# Revit family: Plate_System_Water_Coolers-Zurn-Industries_Z1217
name_source: partatom
category: Plumbing Fixtures
units: mm (PartAtom-declared; Revit-internal decimal feet)

## family parameters
Cut with Voids When Loaded = No
Host = Face
Maintain Annotation Orientation = No
OmniClass Number = 23.45.55.11
OmniClass Title = Sanitary Components
Part Type = Normal
Room Calculation Point = No
Round Connector Dimension = Use Radius
Shared = No

## types (1)
- Z1217
    Approx. Wt. Lbs = 63 "
    Assembly Code = D2030100
    Bolt Material = Steel - Zurn - Stainless - Type - 304
    Bracket Material = Steel - Zurn - Fabricated - Dura-Coated
    CW Connection = No
    CWFU = 0
    Coupling Material = Plastic - Zurn - White
    Default Elevation = 0 "
    Description = Z1217 COUPLING TYPE SYSTEM WALL URINAL / SERVICE SINK
    Flush Flow = 0.0 L/s
    HW Connection = No
    HWFU = 0
    Installation instructions = https://files.zurn.com
    Manufacturer = Zurn Water, LLC
    Manufacturer Brand = Zurn
    Model = Z1217
    Modified Date = 09/25/2025
    Nominal Radius = 2 "
    Product Documentation Link = https://www.zurn.com
    Product Page URL = http://www.zurn.com
    Product data url = https://bimobject.com
    URL = http://www.zurn.com
    Vent Connection = Yes
    Vent Pipe Radius = 1 "
    WFU = 1
    Waste Connection = Yes

## geometry (parser evidence)
native form markers: Blend x8, Sweep x7
no freeform markers — native parametric forms only
